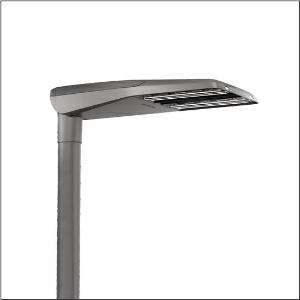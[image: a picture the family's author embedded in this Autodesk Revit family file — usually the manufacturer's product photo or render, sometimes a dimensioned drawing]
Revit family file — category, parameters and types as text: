
# Revit family: streetlight_sl_11_iq_midi___st1_2a_5xc3a31f08me_35e9
name_source: partatom
category: Lighting Fixtures
units: mm (PartAtom-declared; Revit-internal decimal feet)

## family parameters
Cut with Voids When Loaded = No
Host = Face
Light Source = No
Part Type = Normal
Room Calculation Point = No
Round Connector Dimension = Use Diameter
Shared = No

## types (1)
- --- (1 x LED, 15580 lm, 124.7 W, 3000K)
    Apparent Load = 125 VA
    CIE Flux Codes = 32 70 96 100 100
    Color Rendering = 80
    Color Temperature = 3000K
    Default Elevation = 1800 mm
    Description = Streetlight SL 11 iQ midi, mast luminaire, primary light control with 3 zone facetted reflector, of plastic, silver coated, highly specular, primary optical cover: cover, of PMMA, transparent, light distribution: ST1.2a, light emission: direct distribution, primary light characteristic: asymmetric, installation type: post-top, side-entry, LED, High Power LED, rated luminous flux: 15.580lm, luminous efficacy: 125lm/W, light colour: 830, colour temperature: 3000K, control: Street-Remote, optimised constant luminous flux control (CLO 2.0), Desk-Remote (wireless, voltage-free reading and setting of iQ features in the workshop via application-optimized NFC function/RFID function), Light-Fading, Smart-Wire, Night-Set, Lumen-Switch, Temp-Guard, Auto-Match, with cable H07RN-F 5x 1.5mm², mains connection: 230..240V, AC, 50/60Hz, connection cable pre-assembled, cable length: 12,5m, start of lifetime: 125W, end of service life: 132W, reduction: 57W, luminaire housing, of diecast aluminium, powder-coated, Siteco® metallic grey (DB 702S), please order mast flange separately, inclination adjustable without tools: 0°, 5°, 10°, 15° (post-top) | 0°, -5°, -10°, -15° (side-entry), sealing non-destructively replaceable, multi-level sealing system, length: 780mm, width: 376mm, height: 118mm, mast flange for spigot size: 42mm (side-entry): 5XC10008XM4, 60/48mm (side-entry/post-top): 5XC10108XM2, 76/60mm (side-entry/post-top): 5XC10108XM1, equipment: Power, protection rating (complete): IP66, insulation class (complete): insulation class II (safety insulation), certification: CE, ENEC, VDE, impact resistance: IK09, permissible operating ambient temperature for outdoor applications: -25..+50°C, standard-compliant lighting for roads and squares, Environmental Product Declaration (EPD) tested and certified by an independent institute, packaging unit: 1 piece

Light Distribution: ST1.2a
    Height = 118 mm
    Lamp = 1 x LED
    Lamp Light Flux = 15580 lm
    Lamp Power = 124.7 W
    Lamp count = 1
    Length = 780 mm
    Luminous efficacy = 125 lm/W
    Manufacturer = Siteco
    ModVariant = No
    Model = 5XC3A31F08ME
    Number of Poles = 1
    OnlyDefault = Yes
    Power Factor = 1
    Product Name = Streetlight SL 11 iQ midi | ST1.2a
    Product group = mast luminaire | pylon top
    ProductGroupID = 6100
    Protection Class = Protection class II
    Protection Degree = IP 66
    RLX_Detail_Level = 1
    RLX_Emergency_Light_Flux = 0 lm
    RLX_Emergency_Type = 0
    RLX_Emergency_Type_DB = No
    RlxData = <blob elided: 70685 chars, md5=505068eb>
    Socket = socket
    Standby Power = 0 W
    System Light Flux = 15580 lm
    System Power = 125 W
    Type Comments = factory setting: luminous flux: 100 % | dim-lin: 254 | 557 mA
    Type Image = l_1005960.jpg
    URL = http://relux.com
    VarID = @adj_149665
    Voltage = 0 V
    Weight = 0.00 kg
    Width = 376 mm

## geometry (parser evidence)
native form markers: Blend x4, Sweep x10
no freeform markers — native parametric forms only
